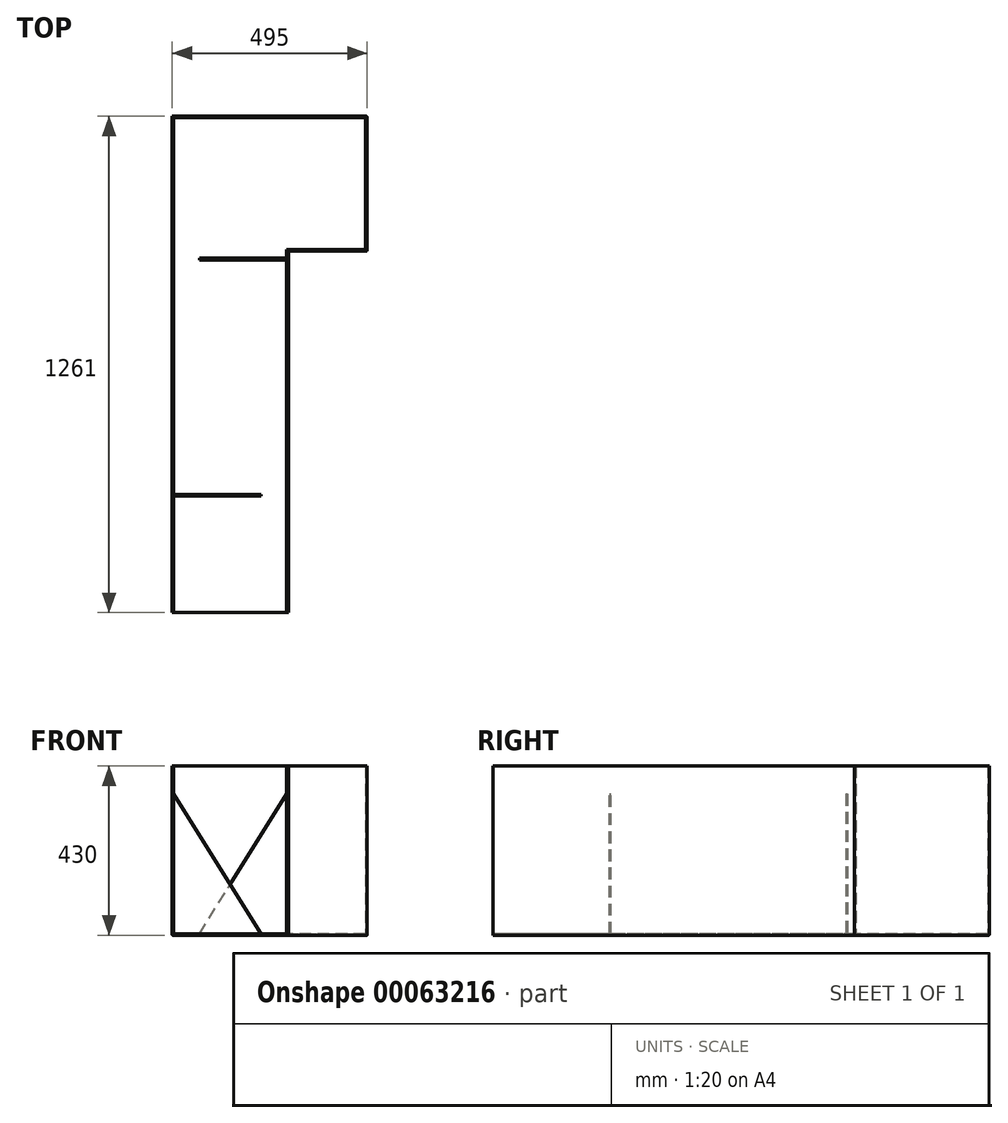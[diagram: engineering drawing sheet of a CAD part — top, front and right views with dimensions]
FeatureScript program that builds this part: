
annotation { "Feature Type Name" : "Feature", "Feature Type Description" : "" }
export const myFeature = defineFeature(function(context is Context, id is Id, definition is map)
    precondition{}
    {
        {
            var Q0;
            Q0=qCreatedBy(makeId("Top.planeOp"),FACE);
            var sketch = newSketch(context, id + "F0", { "sketchPlane" : qUnion([Q0])});
            skLineSegment(sketch, "E0", {"start": v(0, -343) * mm, "end": v(0, 0) * mm});
            skLineSegment(sketch, "E1.MirrorCS", {"start": v(-4, -339) * mm, "end": v(-4, -4) * mm});
            skLineSegment(sketch, "E2.MirrorCS", {"start": v(-4, -4) * mm, "end": v(-491, -4) * mm});
            skLineSegment(sketch, "E3.MirrorCS", {"start": v(0, 0) * mm, "end": v(-495, 0) * mm});
            skLineSegment(sketch, "E4.MirrorCS", {"start": v(-495, 0) * mm, "end": v(-495, -1261) * mm});
            skLineSegment(sketch, "E5.MirrorCS", {"start": v(-491, -4) * mm, "end": v(-491, -1261) * mm});
            skLineSegment(sketch, "E6.MirrorCS", {"start": v(-204, -339) * mm, "end": v(-204, -1261) * mm});
            skLineSegment(sketch, "E7.MirrorCS", {"start": v(-200, -343) * mm, "end": v(-200, -1261) * mm});
            skLineSegment(sketch, "E8.MirrorCS", {"start": v(-200, -343) * mm, "end": v(0, -343) * mm});
            skLineSegment(sketch, "E9.MirrorCS", {"start": v(-204, -339) * mm, "end": v(-4, -339) * mm});
            skLineSegment(sketch, "E10.MirrorCS", {"start": v(-204, -1261) * mm, "end": v(-200, -1261) * mm});
            skLineSegment(sketch, "E11.MirrorCS", {"start": v(-491, -1261) * mm, "end": v(-495, -1261) * mm});
            skSolve(sketch);
        }
        {
            var Q0;
            Q0=makeQuery(id+"F0.imprint","IMPRINT",FACE,{"disambiguationData":[TD([[makeQuery(id+"F0.imprint","IMPRINT",EDGE,{"derivedFrom":sQuery(id+"F0.wireOp",EDGE,"8549452f-c1c4-4c66-b43a-6f4cb653c117")}),-1.0]])]});
            var Q1;
            Q1=makeQuery(id+"F0.imprint","IMPRINT",FACE,{"disambiguationData":[TD([[makeQuery(id+"F0.imprint","IMPRINT",EDGE,{"derivedFrom":sQuery(id+"F0.wireOp",EDGE,"E0")}),1.0]])]});
            extrude(context, id + "F1", {"entities" : qUnion([Q0, Q1]), "depth" : 426 * mm});
        }
        {
            var Q0;
            Q0=qCreatedBy(makeId("Top.planeOp"),FACE);
            var sketch = newSketch(context, id + "F2", { "sketchPlane" : qUnion([Q0])});
            skLineSegment(sketch, "E12.0", {"start": v(-495, 0) * mm, "end": v(-495, -1261) * mm});
            skLineSegment(sketch, "E13.0", {"start": v(-200, -343) * mm, "end": v(-200, -1261) * mm});
            skLineSegment(sketch, "E14.0", {"start": v(-200, -343) * mm, "end": v(0, -343) * mm});
            skLineSegment(sketch, "E15.0", {"start": v(0, -343) * mm, "end": v(0, 0) * mm});
            skLineSegment(sketch, "E16.0", {"start": v(0, 0) * mm, "end": v(-495, 0) * mm});
            skLineSegment(sketch, "E17", {"start": v(-495, -1261) * mm, "end": v(-200, -1261) * mm});
            skSolve(sketch);
        }
        {
            var Q0;
            Q0=qSketchRegion(id+"F2",true);
            extrude(context, id + "F3", {"entities" : qUnion([Q0]), "operationType" : NewBodyOperationType.ADD, "oppositeDirection" : true, "depth" : 4 * mm});
        }
        {
            var Q0;
            Q0=makeQuery(id+"F3.opExtrude","CAP_EDGE",EDGE,{"disambiguationData":[OSD([sQuery(id+"F2.wireOp",EDGE,"e938920c-2318-497f-93e0-1fca7233731b.0")])],"isStart":false});
            var Q1;
            Q1=makeQuery(id+"F3.opExtrude","CAP_EDGE",EDGE,{"disambiguationData":[OSD([sQuery(id+"F2.wireOp",EDGE,"532a1349-e9fd-433e-8e1a-d463d1cb9540.0")])],"isStart":false});
            var Q2;
            Q2=makeQuery(id+"F3.opExtrude","CAP_EDGE",EDGE,{"disambiguationData":[OSD([sQuery(id+"F2.wireOp",EDGE,"f0b50a9b-8d41-4045-a57e-6e178546da08.0")])],"isStart":false});
            var Q3;
            Q3=makeQuery(id+"F3.opExtrude","CAP_EDGE",EDGE,{"disambiguationData":[OSD([sQuery(id+"F2.wireOp",EDGE,"76214740-f755-4499-b80f-307931e5da37.0")])],"isStart":false});
            var Q4;
            Q4=makeQuery(id+"F3.opExtrude","CAP_EDGE",EDGE,{"disambiguationData":[OSD([sQuery(id+"F2.wireOp",EDGE,"6fd2c64b-65cd-4597-b900-bc871f9f6c80.0")])],"isStart":false});
            var Q5;
            Q5=makeQuery(id+"F3.boolean.opBoolean","MERGE",EDGE,{"derivedFrom":[makeQuery(id+"F1.opExtrude","SWEPT_EDGE",EDGE,{"disambiguationData":[OSD([sQuery(id+"F0.wireOp",EDGE,"602087cb-8138-4325-86e3-c2d552e206f1"),sQuery(id+"F0.wireOp",EDGE,"5e85e9da-74ab-4066-82e7-4eeec8f45a40.right")])]}),makeQuery(id+"F3.opExtrude","SWEPT_EDGE",EDGE,{"disambiguationData":[OSD([sQuery(id+"F2.wireOp",EDGE,"532a1349-e9fd-433e-8e1a-d463d1cb9540.0"),sQuery(id+"F2.wireOp",EDGE,"f0b50a9b-8d41-4045-a57e-6e178546da08.0")])]})]});
            var Q6;
            Q6=makeQuery(id+"F3.boolean.opBoolean","MERGE",EDGE,{"derivedFrom":[makeQuery(id+"F1.opExtrude","SWEPT_EDGE",EDGE,{"disambiguationData":[OSD([sQuery(id+"F0.wireOp",EDGE,"602087cb-8138-4325-86e3-c2d552e206f1"),sQuery(id+"F0.wireOp",EDGE,"E0")])]}),makeQuery(id+"F3.opExtrude","SWEPT_EDGE",EDGE,{"disambiguationData":[OSD([sQuery(id+"F2.wireOp",EDGE,"532a1349-e9fd-433e-8e1a-d463d1cb9540.0"),sQuery(id+"F2.wireOp",EDGE,"76214740-f755-4499-b80f-307931e5da37.0")])]})]});
            var Q7;
            Q7=makeQuery(id+"F3.boolean.opBoolean","MERGE",EDGE,{"derivedFrom":[makeQuery(id+"F1.opExtrude","SWEPT_EDGE",EDGE,{"disambiguationData":[OSD([sQuery(id+"F0.wireOp",EDGE,"8549452f-c1c4-4c66-b43a-6f4cb653c117"),sQuery(id+"F0.wireOp",EDGE,"E0")])]}),makeQuery(id+"F3.opExtrude","SWEPT_EDGE",EDGE,{"disambiguationData":[OSD([sQuery(id+"F2.wireOp",EDGE,"76214740-f755-4499-b80f-307931e5da37.0"),sQuery(id+"F2.wireOp",EDGE,"6fd2c64b-65cd-4597-b900-bc871f9f6c80.0")])]})]});
            var Q8;
            Q8=makeQuery(id+"F1.opExtrude","SWEPT_EDGE",EDGE,{"disambiguationData":[OSD([sQuery(id+"F0.wireOp",EDGE,"41269a5a-69f6-4670-b1a7-19bf830e781a"),sQuery(id+"F0.wireOp",EDGE,"c0483dde-b345-4eca-95c5-d6ec0a503eff.right")])]});
            var Q9;
            Q9=makeQuery(id+"F1.opExtrude","SWEPT_EDGE",EDGE,{"disambiguationData":[OSD([sQuery(id+"F0.wireOp",EDGE,"cc5772d9-c29a-4c81-bde5-837d5d9decb7"),sQuery(id+"F0.wireOp",EDGE,"5e85e9da-74ab-4066-82e7-4eeec8f45a40.left")])]});
            var Q10;
            Q10=makeQuery(id+"F1.opExtrude","SWEPT_EDGE",EDGE,{"disambiguationData":[OSD([sQuery(id+"F0.wireOp",EDGE,"41269a5a-69f6-4670-b1a7-19bf830e781a"),sQuery(id+"F0.wireOp",EDGE,"05cfef9b-c223-4bdb-b400-77ea615546ad")])]});
            var Q11;
            Q11=makeQuery(id+"F1.opExtrude","SWEPT_EDGE",EDGE,{"disambiguationData":[OSD([sQuery(id+"F0.wireOp",EDGE,"05cfef9b-c223-4bdb-b400-77ea615546ad"),sQuery(id+"F0.wireOp",EDGE,"cc5772d9-c29a-4c81-bde5-837d5d9decb7")])]});
            var Q12;
            Q12=makeQuery(id+"F3.boolean.opBoolean","MERGE",EDGE,{"derivedFrom":[makeQuery(id+"F1.opExtrude","SWEPT_EDGE",EDGE,{"disambiguationData":[OSD([sQuery(id+"F0.wireOp",EDGE,"8549452f-c1c4-4c66-b43a-6f4cb653c117"),sQuery(id+"F0.wireOp",EDGE,"c0483dde-b345-4eca-95c5-d6ec0a503eff.left")])]}),makeQuery(id+"F3.opExtrude","SWEPT_EDGE",EDGE,{"disambiguationData":[OSD([sQuery(id+"F2.wireOp",EDGE,"6fd2c64b-65cd-4597-b900-bc871f9f6c80.0"),sQuery(id+"F2.wireOp",EDGE,"e938920c-2318-497f-93e0-1fca7233731b.0")])]})]});
            var Q13;
            Q13=makeQuery(id+"F3.opExtrude","CAP_EDGE",EDGE,{"disambiguationData":[OSD([sQuery(id+"F2.wireOp",EDGE,"E13.0")])],"isStart":false});
            var Q14;
            Q14=makeQuery(id+"F3.opExtrude","CAP_EDGE",EDGE,{"disambiguationData":[OSD([sQuery(id+"F2.wireOp",EDGE,"E12.0")])],"isStart":false});
            var Q15;
            Q15=makeQuery(id+"F3.opExtrude","CAP_EDGE",EDGE,{"disambiguationData":[OSD([sQuery(id+"F2.wireOp",EDGE,"E16.0")])],"isStart":false});
            fillet(context, id + "F4", {"entities" : qUnion([Q0, Q1, Q2, Q3, Q4, Q5, Q6, Q7, Q8, Q9, Q10, Q11, Q12, Q13, Q14, Q15]), "radius" : 2 * mm, "tangentPropagation" : true, "allowEdgeOverflow" : false});
        }
        {
            var Q0;
            Q0=makeQuery(id+"F3.boolean.opBoolean","MERGE",FACE,{"derivedFrom":[makeQuery(id+"F1.opExtrude","SWEPT_FACE",FACE,{"disambiguationData":[OSD([sQuery(id+"F0.wireOp",EDGE,"E10.MirrorCS")])]}),makeQuery(id+"F1.opExtrude","SWEPT_FACE",FACE,{"disambiguationData":[OSD([sQuery(id+"F0.wireOp",EDGE,"E11.MirrorCS")])]}),makeQuery(id+"F3.opExtrude","SWEPT_FACE",FACE,{"disambiguationData":[OSD([sQuery(id+"F2.wireOp",EDGE,"E17")])]})]});
            cPlane(context, id + "F5", {"entities" : qUnion([Q0]), "cplaneType" : CPlaneType.OFFSET, "offset" : 300 * mm, "oppositeDirection" : true, "width" : 150 * mm, "height" : 150 * mm});
        }
        {
            var Q0;
            Q0=qCreatedBy(id+"F5.planeOp",FACE);
            var sketch = newSketch(context, id + "F6", { "sketchPlane" : qUnion([Q0])});
            skLineSegment(sketch, "E18", {"start": v(-491, 0) * mm, "end": v(-491, 355) * mm});
            skLineSegment(sketch, "E19", {"start": v(-491, 355) * mm, "end": v(-269, 0) * mm});
            skLineSegment(sketch, "E20", {"start": v(-269, 0) * mm, "end": v(-491, 0) * mm});
            skSolve(sketch);
        }
        {
            var Q0;
            Q0 = qSketchRegion(id + "F6", true);
            extrude(context, id + "F7", {"entities" : qUnion([Q0]), "operationType" : NewBodyOperationType.ADD, "depth" : 4 * mm});
        }
        {
            var Q0;
            Q0=qCreatedBy(id+"F5.planeOp",FACE);
            cPlane(context, id + "F8", {"entities" : qUnion([Q0]), "cplaneType" : CPlaneType.OFFSET, "offset" : 600 * mm, "oppositeDirection" : true, "width" : 150 * mm, "height" : 150 * mm});
        }
        {
            var Q0;
            Q0=qCreatedBy(id+"F8.planeOp",FACE);
            var sketch = newSketch(context, id + "F9", { "sketchPlane" : qUnion([Q0])});
            skLineSegment(sketch, "E21", {"start": v(-204, 0) * mm, "end": v(-426, 0) * mm});
            skLineSegment(sketch, "E22", {"start": v(-426, 0) * mm, "end": v(-204, 355) * mm});
            skLineSegment(sketch, "E23", {"start": v(-204, 355) * mm, "end": v(-204, 0) * mm});
            skSolve(sketch);
        }
        {
            var Q0;
            Q0=makeQuery(id+"F9.imprint","IMPRINT",FACE,{"disambiguationData":[TD([[makeQuery(id+"F9.imprint","IMPRINT",EDGE,{"derivedFrom":sQuery(id+"F9.wireOp",EDGE,"E21")}),-1.0]])]});
            extrude(context, id + "F10", {"entities" : qUnion([Q0]), "depth" : 4 * mm});
        }
    });
